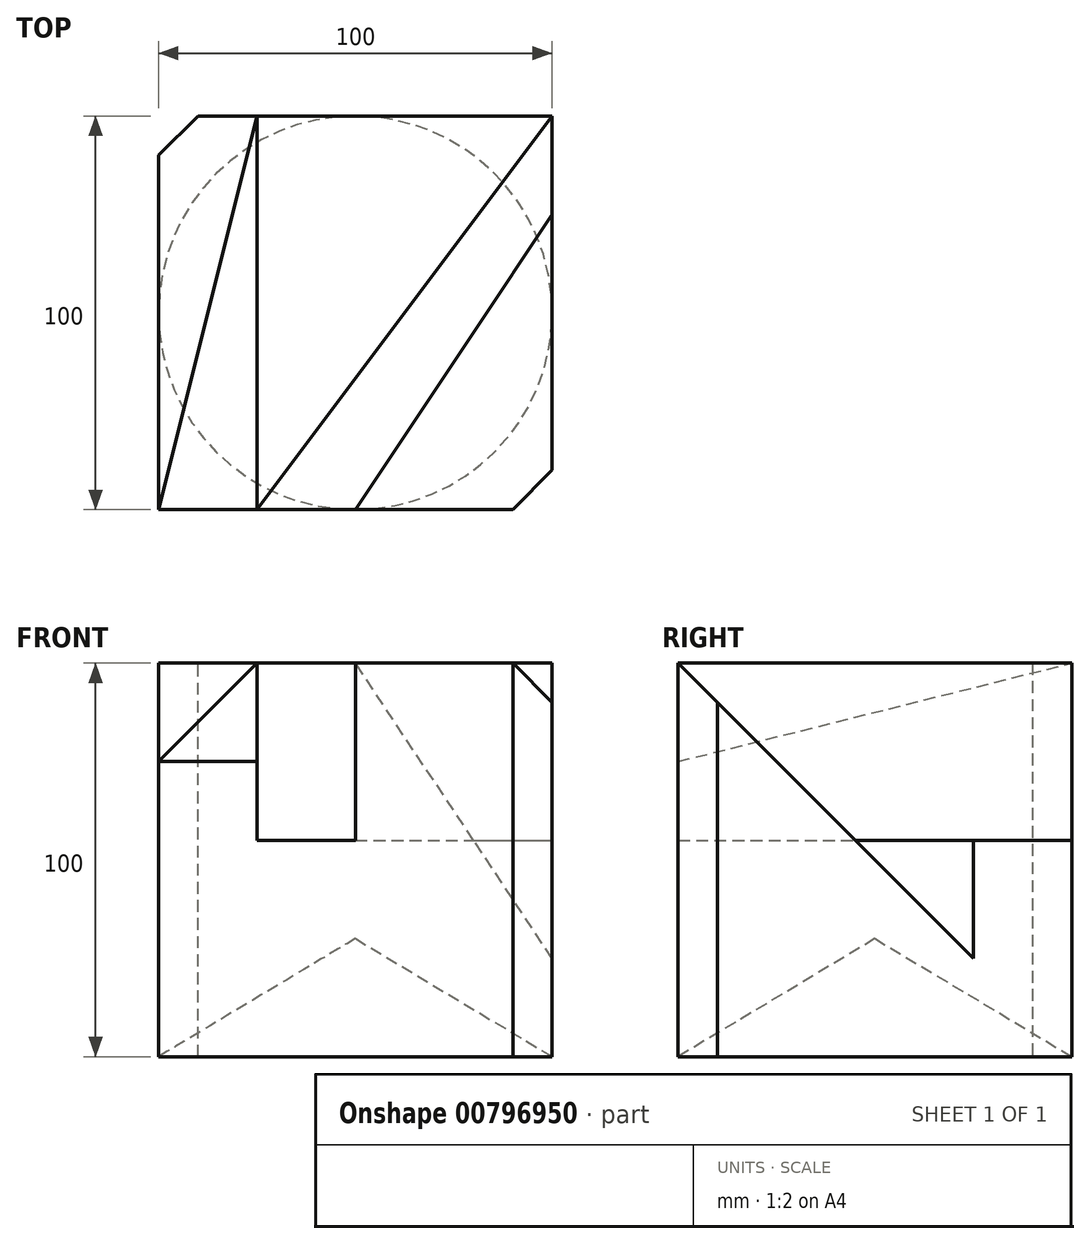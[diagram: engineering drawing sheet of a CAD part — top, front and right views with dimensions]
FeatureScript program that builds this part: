
annotation { "Feature Type Name" : "Feature", "Feature Type Description" : "" }
export const myFeature = defineFeature(function(context is Context, id is Id, definition is map)
    precondition{}
    {
        {
            var Q0;
            Q0=qCreatedBy(makeId("Top.planeOp"),FACE);
            var sketch = newSketch(context, id + "F0", { "sketchPlane" : qUnion([Q0])});
            skLineSegment(sketch, "E0.bottom", {"start": v(100, 100) * mm, "end": v(0, 100) * mm});
            skLineSegment(sketch, "E0.top", {"start": v(100, 0) * mm, "end": v(0, 0) * mm});
            skLineSegment(sketch, "E0.left", {"start": v(100, 100) * mm, "end": v(100, 0) * mm});
            skLineSegment(sketch, "E0.right", {"start": v(0, 100) * mm, "end": v(0, 0) * mm});
            skSolve(sketch);
        }
        {
            var Q0;
            Q0 = qSketchRegion(id + "F0", true);
            extrude(context, id + "F1", {"entities" : qUnion([Q0]), "depth" : 100 * mm, "offsetDistance" : 25 * mm});
        }
        {
            var Q0;
            Q0=makeQuery(id+"F1.opExtrude","SWEPT_EDGE",EDGE,{"disambiguationData":[OSD([sQuery(id+"F0.wireOp",EDGE,"E0.top"),sQuery(id+"F0.wireOp",EDGE,"E0.left")])]});
            var Q1;
            Q1=makeQuery(id+"F1.opExtrude","SWEPT_EDGE",EDGE,{"disambiguationData":[OSD([sQuery(id+"F0.wireOp",EDGE,"E0.bottom"),sQuery(id+"F0.wireOp",EDGE,"E0.right")])]});
            chamfer(context, id + "F2", {"entities" : qUnion([Q0, Q1]), "width" : 10 * mm, "tangentPropagation" : true});
        }
        {
            var Q0;
            Q0=makeQuery(id+"F1.opExtrude","SWEPT_FACE",FACE,{"disambiguationData":[OSD([sQuery(id+"F0.wireOp",EDGE,"E0.top")])]});
            var sketch = newSketch(context, id + "F3", { "sketchPlane" : qUnion([Q0])});
            skLineSegment(sketch, "E1.bottom", {"start": v(0, 100) * mm, "end": v(25, 100) * mm});
            skLineSegment(sketch, "E1.top", {"start": v(0, 75) * mm, "end": v(25, 75) * mm});
            skLineSegment(sketch, "E1.left", {"start": v(0, 100) * mm, "end": v(0, 75) * mm});
            skLineSegment(sketch, "E1.right", {"start": v(25, 100) * mm, "end": v(25, 75) * mm});
            skSolve(sketch);
        }
        {
            var Q0;
            Q0=makeQuery(id+"F1.opExtrude","CAP_FACE",FACE,{"disambiguationData":[OSD([sQuery(id+"F0.wireOp",EDGE,"E0.bottom"),sQuery(id+"F0.wireOp",EDGE,"E0.top"),sQuery(id+"F0.wireOp",EDGE,"E0.left"),sQuery(id+"F0.wireOp",EDGE,"E0.right")])],"isStart":false});
            var sketch = newSketch(context, id + "F4", { "sketchPlane" : qUnion([Q0])});
            skPoint(sketch, "E2", {"position": v(25, 100) * mm});
            skSolve(sketch);
        }
        {
            var Q1;
            Q1=makeQuery(id+"F3.imprint","IMPRINT",FACE,{"disambiguationData":[TD([[makeQuery(id+"F3.imprint","IMPRINT",EDGE,{"derivedFrom":sQuery(id+"F3.wireOp",EDGE,"E1.bottom")}),1.0]])]});
            var Q2;
            Q2=sQuery(id+"F4.wireOp",VERTEX,"E2");
            loft(context, id + "F5", {"operationType" : NewBodyOperationType.REMOVE, "sheetProfilesArray" : [{ "sheetProfileEntities" : qUnion([Q1]) }, { "sheetProfileEntities" : qUnion([Q2]) }]});
        }
        {
            var Q0;
            Q0=qCreatedBy(makeId("Top.planeOp"),FACE);
            cPlane(context, id + "F6", {"entities" : qUnion([Q0]), "cplaneType" : CPlaneType.OFFSET, "offset" : 30 * mm, "width" : 150 * mm, "height" : 150 * mm});
        }
        {
            var Q0;
            Q0=qCreatedBy(id+"F6.planeOp",FACE);
            var sketch = newSketch(context, id + "F7", { "sketchPlane" : qUnion([Q0])});
            skPoint(sketch, "E3", {"position": v(50, 50) * mm});
            skSolve(sketch);
        }
        {
            var Q0;
            Q0=makeQuery(id+"F1.opExtrude","CAP_FACE",FACE,{"disambiguationData":[OSD([sQuery(id+"F0.wireOp",EDGE,"E0.bottom"),sQuery(id+"F0.wireOp",EDGE,"E0.top"),sQuery(id+"F0.wireOp",EDGE,"E0.left"),sQuery(id+"F0.wireOp",EDGE,"E0.right")])],"isStart":true});
            var sketch = newSketch(context, id + "F8", { "sketchPlane" : qUnion([Q0])});
            skCircle(sketch, "E4", {"center": v(50, -50) * mm, "radius": 50 * mm});
            skSolve(sketch);
        }
        {
            var Q1;
            {var subQ0=sQuery(id+"F8.wireOp",EDGE,"E4");var subQ1=makeQuery(id+"F8.imprint","INTERSECT",VERTEX,{"derivedFrom":[makeQuery(id+"F1.opExtrude","CAP_EDGE",EDGE,{"disambiguationData":[OSD([sQuery(id+"F0.wireOp",EDGE,"E0.top")])],"isStart":true}),subQ0]});Q1=makeQuery(id+"F8.imprint","IMPRINT",FACE,{"disambiguationData":[TD([[makeQuery(id+"F8.imprint","IMPRINT",EDGE,{"disambiguationData":[TD([[subQ1,1.0]])],"derivedFrom":subQ0}),1.0]])]});}
            var Q2;
            Q2=sQuery(id+"F7.wireOp",VERTEX,"E3");
            loft(context, id + "F9", {"operationType" : NewBodyOperationType.REMOVE, "sheetProfilesArray" : [{ "sheetProfileEntities" : qUnion([Q1]) }, { "sheetProfileEntities" : qUnion([Q2]) }]});
        }
        {
            var Q0;
            {var subQ0=sQuery(id+"F0.wireOp",EDGE,"E0.left");var subQ4=sQuery(id+"F0.wireOp",EDGE,"E0.top");var subQ6=sQuery(id+"F0.wireOp",EDGE,"E0.right");var subQ7=sQuery(id+"F0.wireOp",EDGE,"E0.bottom");var subQ8=makeQuery(id+"F1.opExtrude","CAP_FACE",FACE,{"disambiguationData":[OSD([subQ7,subQ4,subQ0,subQ6])],"isStart":false});Q0=makeQuery(id+"F5.boolean.opBoolean","SPLIT",FACE,{"disambiguationData":[TD([makeQuery(id+"F1.opExtrude","SWEPT_FACE",FACE,{"disambiguationData":[OSD([subQ4])]})])],"derivedFrom":subQ8});}
            var sketch = newSketch(context, id + "F10", { "sketchPlane" : qUnion([Q0])});
            skLineSegment(sketch, "E5", {"start": v(25, 0) * mm, "end": v(100, 100) * mm});
            skLineSegment(sketch, "E6", {"start": v(50, 0) * mm, "end": v(100, 75) * mm});
            skLineSegment(sketch, "E7", {"start": v(100, 75) * mm, "end": v(100, 100) * mm});
            skLineSegment(sketch, "E8", {"start": v(50, 0) * mm, "end": v(25, 0) * mm});
            skSolve(sketch);
        }
        {
            var Q0;
            Q0 = qSketchRegion(id + "F10", true);
            extrude(context, id + "F11", {"entities" : qUnion([Q0]), "operationType" : NewBodyOperationType.REMOVE, "oppositeDirection" : true, "depth" : 45 * mm, "offsetDistance" : 25 * mm});
        }
        {
            var Q0;
            Q0=makeQuery(id+"F1.opExtrude","SWEPT_FACE",FACE,{"disambiguationData":[OSD([sQuery(id+"F0.wireOp",EDGE,"E0.left")])]});
            var sketch = newSketch(context, id + "F12", { "sketchPlane" : qUnion([Q0])});
            skLineSegment(sketch, "E9", {"start": v(0, 100) * mm, "end": v(75, 25) * mm});
            skLineSegment(sketch, "E10", {"start": v(75, 25) * mm, "end": v(75, 55) * mm});
            skLineSegment(sketch, "E11", {"start": v(0, 100) * mm, "end": v(75, 100) * mm});
            skLineSegment(sketch, "E12", {"start": v(75, 100) * mm, "end": v(75, 55) * mm});
            skSolve(sketch);
        }
        {
            var Q0;
            Q0 = qSketchRegion(id + "F12", true);
            var Q1;
            Q1=makeQuery(id+"F11.boolean.opBoolean","COPY",FACE,{"derivedFrom":makeQuery(id+"F11.opExtrude","SWEPT_FACE",FACE,{"disambiguationData":[OSD([sQuery(id+"F10.wireOp",EDGE,"E6")])]})});
            extrude(context, id + "F13", {"entities" : qUnion([Q0]), "operationType" : NewBodyOperationType.REMOVE, "endBound" : BoundingType.UP_TO_SURFACE, "oppositeDirection" : true, "depth" : 25 * mm, "endBoundEntityFace" : qUnion([Q1]), "offsetDistance" : 25 * mm});
        }
    });
